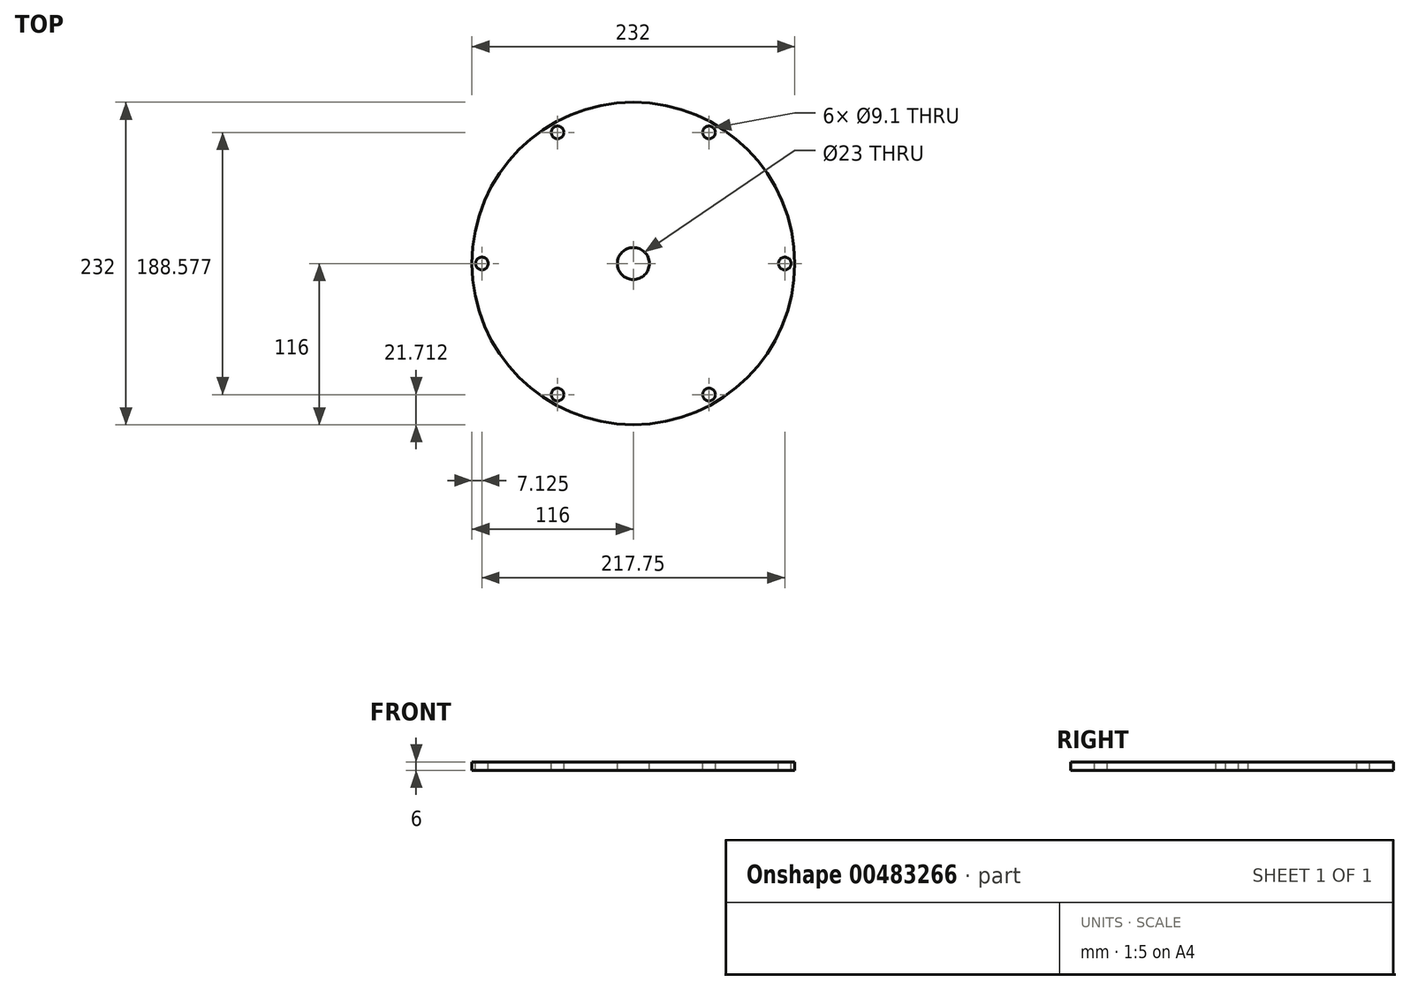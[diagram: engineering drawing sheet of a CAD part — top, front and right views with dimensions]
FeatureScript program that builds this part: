
annotation { "Feature Type Name" : "Feature", "Feature Type Description" : "" }
export const myFeature = defineFeature(function(context is Context, id is Id, definition is map)
    precondition{}
    {
        {
            var Q0;
            Q0=qCreatedBy(makeId("Top.planeOp"),FACE);
            var sketch = newSketch(context, id + "F0", { "sketchPlane" : qUnion([Q0])});
            skCircle(sketch, "E0", {"center": v(0, 0) * mm, "radius": 116 * mm});
            skSolve(sketch);
        }
        {
            var Q0;
            Q0=makeQuery(id+"F0.imprint","IMPRINT",FACE,{"disambiguationData":[TD([[makeQuery(id+"F0.imprint","IMPRINT",EDGE,{"derivedFrom":sQuery(id+"F0.wireOp",EDGE,"E0")}),1.0]])]});
            extrude(context, id + "F1", {"entities" : qUnion([Q0]), "depth" : 6 * mm, "offsetDistance" : 25 * mm});
        }
        {
            var Q0;
            Q0=makeQuery(id+"F1.opExtrude","CAP_FACE",FACE,{"disambiguationData":[OSD([sQuery(id+"F0.wireOp",EDGE,"E0")])],"isStart":false});
            var sketch = newSketch(context, id + "F2", { "sketchPlane" : qUnion([Q0])});
            skCircle(sketch, "E1.cCircle", {"center": v(0, 0) * mm, "radius": 108.88 * mm, "construction": true});
            skLineSegment(sketch, "E1.0", {"start": v(-108.88, 0) * mm, "end": v(-54.44, 94.29) * mm});
            skLineSegment(sketch, "E1.1", {"start": v(-54.44, 94.29) * mm, "end": v(54.44, 94.29) * mm});
            skLineSegment(sketch, "E1.2", {"start": v(54.44, 94.29) * mm, "end": v(108.88, 0) * mm});
            skLineSegment(sketch, "E1.3", {"start": v(108.88, 0) * mm, "end": v(54.44, -94.29) * mm});
            skLineSegment(sketch, "E1.4", {"start": v(54.44, -94.29) * mm, "end": v(-54.44, -94.29) * mm});
            skLineSegment(sketch, "E1.5", {"start": v(-54.44, -94.29) * mm, "end": v(-108.88, 0) * mm});
            skSolve(sketch);
        }
        {
            var Q0;
            Q0=sQuery(id+"F2.wireOp",VERTEX,"E1.1.start");
            var Q1;
            Q1=sQuery(id+"F2.wireOp",VERTEX,"E1.2.start");
            var Q2;
            Q2=sQuery(id+"F2.wireOp",VERTEX,"E1.3.start");
            var Q3;
            Q3=sQuery(id+"F2.wireOp",VERTEX,"E1.4.start");
            var Q4;
            Q4=sQuery(id+"F2.wireOp",VERTEX,"E1.5.start");
            var Q5;
            Q5=sQuery(id+"F2.wireOp",VERTEX,"E1.0.start");
            var Q6;
            Q6=makeQuery(id+"F1.opExtrude","SWEPT_BODY",BODY,{"disambiguationData":[OSD([sQuery(id+"F0.wireOp",EDGE,"E0")])]});
            hole(context, id + "F3", {"style" : HoleStyle.SIMPLE, "endStyle" : HoleEndStyle.THROUGH, "holeDiameter" : 9.1 * mm, "isTappedThrough" : true, "tappedDepth" : 12 * mm, "tapClearance" : 3, "locations" : qUnion([Q0, Q1, Q2, Q3, Q4, Q5]), "scope" : qUnion([Q6])});
        }
        {
            var Q0;
            Q0=makeQuery(id+"F1.opExtrude","CAP_FACE",FACE,{"disambiguationData":[OSD([sQuery(id+"F0.wireOp",EDGE,"E0")])],"isStart":false});
            var sketch = newSketch(context, id + "F4", { "sketchPlane" : qUnion([Q0])});
            skPoint(sketch, "E2", {"position": v(0, 0) * mm});
            skSolve(sketch);
        }
        {
            var Q0;
            Q0=sQuery(id+"F4.wireOp",VERTEX,"E2");
            var Q1;
            Q1=makeQuery(id+"F1.opExtrude","SWEPT_BODY",BODY,{"disambiguationData":[OSD([sQuery(id+"F0.wireOp",EDGE,"E0")])]});
            hole(context, id + "F5", {"style" : HoleStyle.SIMPLE, "endStyle" : HoleEndStyle.THROUGH, "holeDiameter" : 23 * mm, "isTappedThrough" : true, "tappedDepth" : 12 * mm, "tapClearance" : 3, "locations" : qUnion([Q0]), "scope" : qUnion([Q1])});
        }
    });
